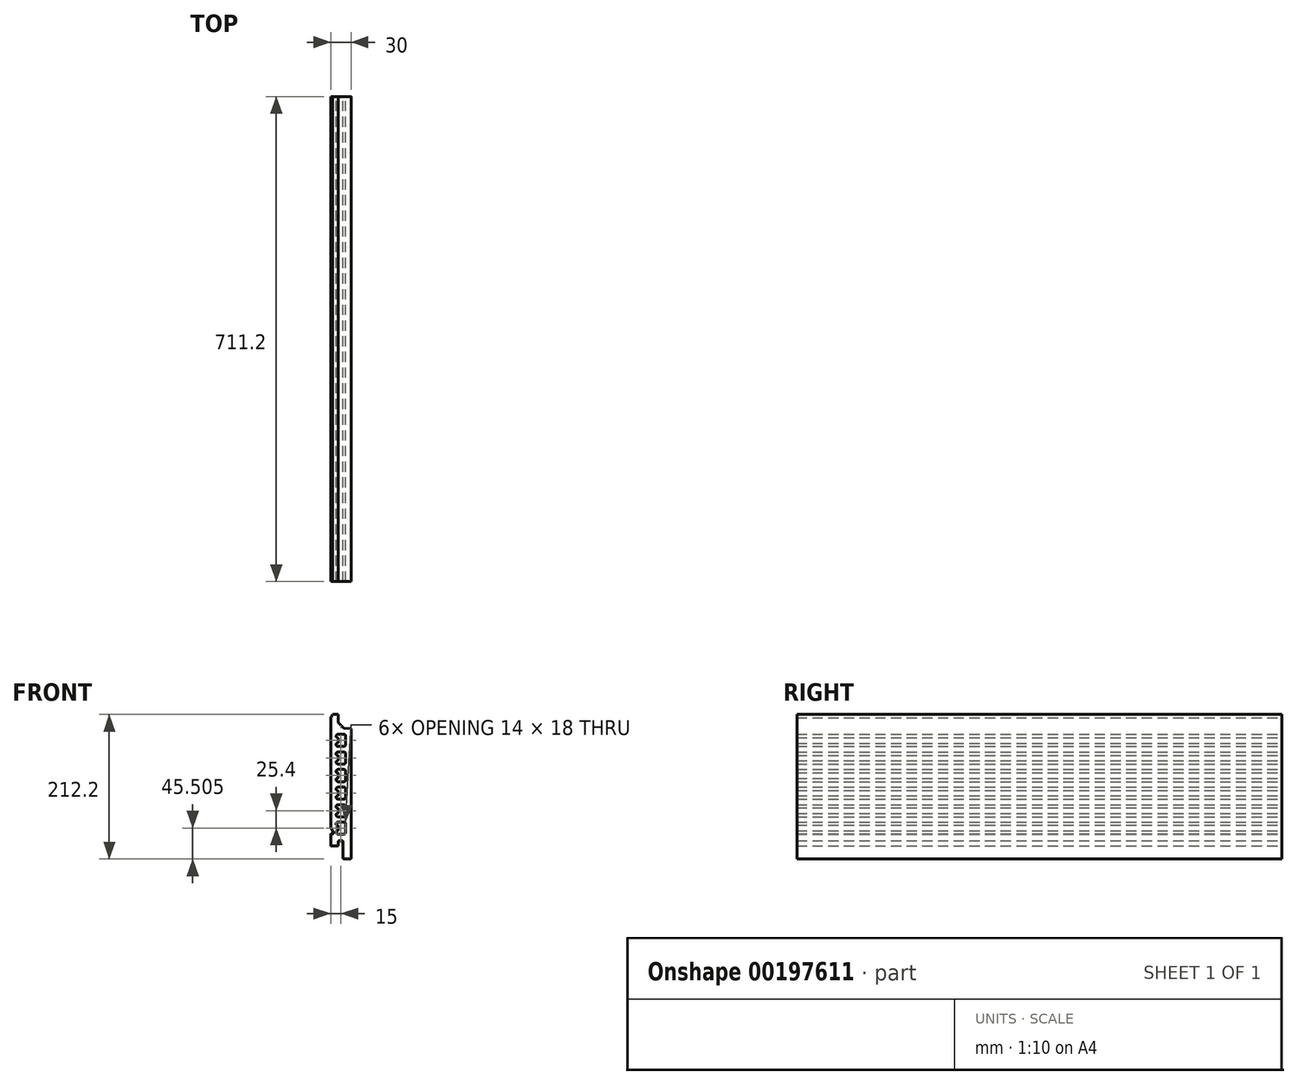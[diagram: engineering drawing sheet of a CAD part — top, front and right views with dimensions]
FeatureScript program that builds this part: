
annotation { "Feature Type Name" : "Feature", "Feature Type Description" : "" }
export const myFeature = defineFeature(function(context is Context, id is Id, definition is map)
    precondition{}
    {
        {
            var Q0;
            Q0=qCreatedBy(makeId("Front.planeOp"),FACE);
            var sketch = newSketch(context, id + "F0", { "sketchPlane" : qUnion([Q0])});
            skLineSegment(sketch, "E0", {"start": v(-14.86, -59.63) * mm, "end": v(-11.1, -67.7) * mm});
            skArc(sketch, "E1", {"start": v(-11.1, -67.7) * mm, "mid": v(-11.16, -68.66) * mm, "end": v(-12, -69.12) * mm});
            skLineSegment(sketch, "E2", {"start": v(-12, -69.12) * mm, "end": v(-14, -69.12) * mm});
            skArc(sketch, "E3", {"start": v(-14, -69.12) * mm, "mid": v(-14.7, -69.41) * mm, "end": v(-15, -70.12) * mm});
            skLineSegment(sketch, "E4", {"start": v(-15, -70.12) * mm, "end": v(-15, -85.6) * mm});
            skArc(sketch, "E5", {"start": v(-15, -85.6) * mm, "mid": v(-14.56, -86.66) * mm, "end": v(-13.5, -87.1) * mm});
            skLineSegment(sketch, "E6", {"start": v(-13.5, -87.1) * mm, "end": v(-5.5, -87.1) * mm});
            skArc(sketch, "E7", {"start": v(-5.5, -87.1) * mm, "mid": v(-4.44, -86.66) * mm, "end": v(-4, -85.6) * mm});
            skLineSegment(sketch, "E8", {"start": v(-4, -85.6) * mm, "end": v(-4, -80.6) * mm});
            skArc(sketch, "E9", {"start": v(-4, -80.6) * mm, "mid": v(-3.56, -79.54) * mm, "end": v(-2.5, -79.1) * mm});
            skLineSegment(sketch, "E10", {"start": v(-2.5, -79.1) * mm, "end": v(1.48, -79.1) * mm});
            skArc(sketch, "E11", {"start": v(1.48, -79.1) * mm, "mid": v(2.54, -79.54) * mm, "end": v(2.98, -80.6) * mm});
            skLineSegment(sketch, "E12", {"start": v(2.98, -80.6) * mm, "end": v(2.98, -104.6) * mm});
            skArc(sketch, "E13", {"start": v(2.98, -104.6) * mm, "mid": v(3.42, -105.66) * mm, "end": v(4.48, -106.1) * mm});
            skLineSegment(sketch, "E14", {"start": v(4.48, -106.1) * mm, "end": v(13.5, -106.1) * mm});
            skArc(sketch, "E15", {"start": v(13.5, -106.1) * mm, "mid": v(14.56, -105.66) * mm, "end": v(15, -104.6) * mm});
            skLineSegment(sketch, "E16", {"start": v(15, -104.6) * mm, "end": v(15, 83.78) * mm});
            skArc(sketch, "E17", {"start": v(15, 83.78) * mm, "mid": v(14.58, 84.81) * mm, "end": v(13.57, 85.27) * mm});
            skLineSegment(sketch, "E18", {"start": v(13.57, 85.27) * mm, "end": v(5.1, 85.66) * mm});
            skArc(sketch, "E19", {"start": v(5.1, 85.66) * mm, "mid": v(4.57, 85.79) * mm, "end": v(4.11, 86.1) * mm});
            skLineSegment(sketch, "E20", {"start": v(4.11, 86.1) * mm, "end": v(-3.56, 93.77) * mm});
            skArc(sketch, "E21", {"start": v(-3.56, 93.77) * mm, "mid": v(-3.89, 94.26) * mm, "end": v(-4, 94.83) * mm});
            skLineSegment(sketch, "E22", {"start": v(-4, 94.83) * mm, "end": v(-4, 106.1) * mm});
            skLineSegment(sketch, "E23", {"start": v(-4, 106.1) * mm, "end": v(-12.31, 106.1) * mm});
            skLineSegment(sketch, "E24", {"start": v(-12.31, 106.1) * mm, "end": v(-15, 101.2) * mm});
            skLineSegment(sketch, "E25", {"start": v(-15, 101.2) * mm, "end": v(-15, -59) * mm});
            skArc(sketch, "E26", {"start": v(-15, -59) * mm, "mid": v(-14.96, -59.32) * mm, "end": v(-14.86, -59.63) * mm});
            skArc(sketch, "E27", {"start": v(-14.86, -59.63) * mm, "mid": v(-14.96, -59.32) * mm, "end": v(-15, -59) * mm});
            skSolve(sketch);
        }
        {
            var Q0;
            Q0=makeQuery(id+"F0.imprint","IMPRINT",FACE,{"disambiguationData":[TD([[makeQuery(id+"F0.imprint","IMPRINT",EDGE,{"derivedFrom":sQuery(id+"F0.wireOp",EDGE,"E3")}),1.0]])]});
            extrude(context, id + "F1", {"entities" : qUnion([Q0]), "depth" : 711.2 * mm});
        }
        {
            var Q0;
            Q0=qCreatedBy(makeId("Front.planeOp"),FACE);
            var sketch = newSketch(context, id + "F2", { "sketchPlane" : qUnion([Q0])});
            skArc(sketch, "E28", {"start": v(-4, -32.7) * mm, "mid": v(-4.43, -31.63) * mm, "end": v(-5.5, -31.2) * mm});
            skLineSegment(sketch, "E29", {"start": v(-5.5, -31.2) * mm, "end": v(-5.5, -31.2) * mm});
            skArc(sketch, "E30", {"start": v(-5.5, -31.2) * mm, "mid": v(-6.56, -30.76) * mm, "end": v(-7, -29.7) * mm});
            skLineSegment(sketch, "E31", {"start": v(-7, -29.7) * mm, "end": v(-7, -29.2) * mm});
            skArc(sketch, "E32", {"start": v(-7, -29.2) * mm, "mid": v(-6.12, -27.07) * mm, "end": v(-4, -26.2) * mm});
            skLineSegment(sketch, "E33", {"start": v(-4, -26.2) * mm, "end": v(4, -26.2) * mm});
            skArc(sketch, "E34", {"start": v(4, -26.2) * mm, "mid": v(6.12, -27.07) * mm, "end": v(7, -29.2) * mm});
            skLineSegment(sketch, "E35", {"start": v(7, -29.2) * mm, "end": v(7, -41.2) * mm});
            skArc(sketch, "E36", {"start": v(7, -41.2) * mm, "mid": v(6.12, -43.32) * mm, "end": v(4, -44.2) * mm});
            skLineSegment(sketch, "E37", {"start": v(4, -44.2) * mm, "end": v(-4, -44.2) * mm});
            skArc(sketch, "E38", {"start": v(-4, -44.2) * mm, "mid": v(-6.12, -43.32) * mm, "end": v(-7, -41.2) * mm});
            skLineSegment(sketch, "E39", {"start": v(-7, -41.2) * mm, "end": v(-7, -40.7) * mm});
            skArc(sketch, "E40", {"start": v(-7, -40.7) * mm, "mid": v(-6.56, -39.63) * mm, "end": v(-5.5, -39.2) * mm});
            skLineSegment(sketch, "E41", {"start": v(-5.5, -39.2) * mm, "end": v(-5.5, -39.2) * mm});
            skArc(sketch, "E42", {"start": v(-5.5, -39.2) * mm, "mid": v(-4.43, -38.76) * mm, "end": v(-4, -37.7) * mm});
            skLineSegment(sketch, "E43", {"start": v(-4, -37.7) * mm, "end": v(-4, -32.7) * mm});
            skArc(sketch, "E44", {"start": v(-4, -58.1) * mm, "mid": v(-4.43, -57.03) * mm, "end": v(-5.5, -56.6) * mm});
            skLineSegment(sketch, "E45", {"start": v(-5.5, -56.6) * mm, "end": v(-5.5, -56.6) * mm});
            skArc(sketch, "E46", {"start": v(-5.5, -56.6) * mm, "mid": v(-6.56, -56.16) * mm, "end": v(-7, -55.1) * mm});
            skLineSegment(sketch, "E47", {"start": v(-7, -55.1) * mm, "end": v(-7, -54.6) * mm});
            skArc(sketch, "E48", {"start": v(-7, -54.6) * mm, "mid": v(-6.12, -52.47) * mm, "end": v(-4, -51.6) * mm});
            skLineSegment(sketch, "E49", {"start": v(-4, -51.6) * mm, "end": v(4, -51.6) * mm});
            skArc(sketch, "E50", {"start": v(4, -51.6) * mm, "mid": v(6.12, -52.47) * mm, "end": v(7, -54.6) * mm});
            skLineSegment(sketch, "E51", {"start": v(7, -54.6) * mm, "end": v(7, -66.6) * mm});
            skArc(sketch, "E52", {"start": v(7, -66.6) * mm, "mid": v(6.12, -68.72) * mm, "end": v(4, -69.6) * mm});
            skLineSegment(sketch, "E53", {"start": v(4, -69.6) * mm, "end": v(-4, -69.6) * mm});
            skArc(sketch, "E54", {"start": v(-4, -69.6) * mm, "mid": v(-6.12, -68.72) * mm, "end": v(-7, -66.6) * mm});
            skLineSegment(sketch, "E55", {"start": v(-7, -66.6) * mm, "end": v(-7, -66.1) * mm});
            skArc(sketch, "E56", {"start": v(-7, -66.1) * mm, "mid": v(-6.56, -65.03) * mm, "end": v(-5.5, -64.6) * mm});
            skLineSegment(sketch, "E57", {"start": v(-5.5, -64.6) * mm, "end": v(-5.5, -64.6) * mm});
            skArc(sketch, "E58", {"start": v(-5.5, -64.6) * mm, "mid": v(-4.43, -64.16) * mm, "end": v(-4, -63.1) * mm});
            skLineSegment(sketch, "E59", {"start": v(-4, -63.1) * mm, "end": v(-4, -58.1) * mm});
            skArc(sketch, "E60", {"start": v(-4, -6.9) * mm, "mid": v(-4.43, -5.83) * mm, "end": v(-5.5, -5.4) * mm});
            skLineSegment(sketch, "E61", {"start": v(-5.5, -5.4) * mm, "end": v(-5.5, -5.4) * mm});
            skArc(sketch, "E62", {"start": v(-5.5, -5.4) * mm, "mid": v(-6.56, -4.96) * mm, "end": v(-7, -3.9) * mm});
            skLineSegment(sketch, "E63", {"start": v(-7, -3.9) * mm, "end": v(-7, -3.4) * mm});
            skArc(sketch, "E64", {"start": v(-7, -3.4) * mm, "mid": v(-6.12, -1.27) * mm, "end": v(-4, -0.4) * mm});
            skLineSegment(sketch, "E65", {"start": v(-4, -0.4) * mm, "end": v(4, -0.4) * mm});
            skArc(sketch, "E66", {"start": v(4, -0.4) * mm, "mid": v(6.12, -1.27) * mm, "end": v(7, -3.4) * mm});
            skLineSegment(sketch, "E67", {"start": v(7, -3.4) * mm, "end": v(7, -15.4) * mm});
            skArc(sketch, "E68", {"start": v(7, -15.4) * mm, "mid": v(6.12, -17.52) * mm, "end": v(4, -18.4) * mm});
            skLineSegment(sketch, "E69", {"start": v(4, -18.4) * mm, "end": v(-4, -18.4) * mm});
            skArc(sketch, "E70", {"start": v(-4, -18.4) * mm, "mid": v(-6.12, -17.52) * mm, "end": v(-7, -15.4) * mm});
            skLineSegment(sketch, "E71", {"start": v(-7, -15.4) * mm, "end": v(-7, -14.9) * mm});
            skArc(sketch, "E72", {"start": v(-7, -14.9) * mm, "mid": v(-6.56, -13.83) * mm, "end": v(-5.5, -13.4) * mm});
            skLineSegment(sketch, "E73", {"start": v(-5.5, -13.4) * mm, "end": v(-5.5, -13.4) * mm});
            skArc(sketch, "E74", {"start": v(-5.5, -13.4) * mm, "mid": v(-4.43, -12.96) * mm, "end": v(-4, -11.9) * mm});
            skLineSegment(sketch, "E75", {"start": v(-4, -11.9) * mm, "end": v(-4, -6.9) * mm});
            skLineSegment(sketch, "E76", {"start": v(-5.5, 20.4) * mm, "end": v(-5.5, 20.4) * mm});
            skArc(sketch, "E77", {"start": v(-5.5, 20.4) * mm, "mid": v(-6.56, 20.84) * mm, "end": v(-7, 21.9) * mm});
            skLineSegment(sketch, "E78", {"start": v(-7, 21.9) * mm, "end": v(-7, 22.4) * mm});
            skArc(sketch, "E79", {"start": v(-7, 22.4) * mm, "mid": v(-6.12, 24.52) * mm, "end": v(-4, 25.4) * mm});
            skLineSegment(sketch, "E80", {"start": v(-4, 25.4) * mm, "end": v(4, 25.4) * mm});
            skArc(sketch, "E81", {"start": v(4, 25.4) * mm, "mid": v(6.12, 24.52) * mm, "end": v(7, 22.4) * mm});
            skLineSegment(sketch, "E82", {"start": v(7, 22.4) * mm, "end": v(7, 10.4) * mm});
            skArc(sketch, "E83", {"start": v(7, 10.4) * mm, "mid": v(6.12, 8.28) * mm, "end": v(4, 7.4) * mm});
            skLineSegment(sketch, "E84", {"start": v(4, 7.4) * mm, "end": v(-4, 7.4) * mm});
            skArc(sketch, "E85", {"start": v(-4, 7.4) * mm, "mid": v(-6.12, 8.28) * mm, "end": v(-7, 10.4) * mm});
            skLineSegment(sketch, "E86", {"start": v(-7, 10.4) * mm, "end": v(-7, 10.9) * mm});
            skArc(sketch, "E87", {"start": v(-7, 10.9) * mm, "mid": v(-6.56, 11.96) * mm, "end": v(-5.5, 12.4) * mm});
            skLineSegment(sketch, "E88", {"start": v(-5.5, 12.4) * mm, "end": v(-5.5, 12.4) * mm});
            skArc(sketch, "E89", {"start": v(-5.5, 12.4) * mm, "mid": v(-4.43, 12.84) * mm, "end": v(-4, 13.9) * mm});
            skLineSegment(sketch, "E90", {"start": v(-4, 13.9) * mm, "end": v(-4, 18.9) * mm});
            skArc(sketch, "E91", {"start": v(-4, 18.9) * mm, "mid": v(-4.43, 19.96) * mm, "end": v(-5.5, 20.4) * mm});
            skLineSegment(sketch, "E92", {"start": v(-5.5, 46.2) * mm, "end": v(-5.5, 46.2) * mm});
            skArc(sketch, "E93", {"start": v(-5.5, 46.2) * mm, "mid": v(-6.56, 46.64) * mm, "end": v(-7, 47.7) * mm});
            skLineSegment(sketch, "E94", {"start": v(-7, 47.7) * mm, "end": v(-7, 48.2) * mm});
            skArc(sketch, "E95", {"start": v(-7, 48.2) * mm, "mid": v(-6.12, 50.32) * mm, "end": v(-4, 51.2) * mm});
            skLineSegment(sketch, "E96", {"start": v(-4, 51.2) * mm, "end": v(4, 51.2) * mm});
            skArc(sketch, "E97", {"start": v(4, 51.2) * mm, "mid": v(6.12, 50.32) * mm, "end": v(7, 48.2) * mm});
            skLineSegment(sketch, "E98", {"start": v(7, 48.2) * mm, "end": v(7, 36.2) * mm});
            skArc(sketch, "E99", {"start": v(7, 36.2) * mm, "mid": v(6.12, 34.08) * mm, "end": v(4, 33.2) * mm});
            skLineSegment(sketch, "E100", {"start": v(4, 33.2) * mm, "end": v(-4, 33.2) * mm});
            skArc(sketch, "E101", {"start": v(-4, 33.2) * mm, "mid": v(-6.12, 34.08) * mm, "end": v(-7, 36.2) * mm});
            skLineSegment(sketch, "E102", {"start": v(-7, 36.2) * mm, "end": v(-7, 36.7) * mm});
            skArc(sketch, "E103", {"start": v(-7, 36.7) * mm, "mid": v(-6.56, 37.76) * mm, "end": v(-5.5, 38.2) * mm});
            skLineSegment(sketch, "E104", {"start": v(-5.5, 38.2) * mm, "end": v(-5.5, 38.2) * mm});
            skArc(sketch, "E105", {"start": v(-5.5, 38.2) * mm, "mid": v(-4.43, 38.64) * mm, "end": v(-4, 39.7) * mm});
            skLineSegment(sketch, "E106", {"start": v(-4, 39.7) * mm, "end": v(-4, 44.7) * mm});
            skArc(sketch, "E107", {"start": v(-4, 44.7) * mm, "mid": v(-4.43, 45.76) * mm, "end": v(-5.5, 46.2) * mm});
            skLineSegment(sketch, "E108", {"start": v(-5.5, 72) * mm, "end": v(-5.5, 72) * mm});
            skArc(sketch, "E109", {"start": v(-5.5, 72) * mm, "mid": v(-6.56, 72.43) * mm, "end": v(-7, 73.5) * mm});
            skLineSegment(sketch, "E110", {"start": v(-7, 73.5) * mm, "end": v(-7, 74) * mm});
            skArc(sketch, "E111", {"start": v(-7, 74) * mm, "mid": v(-6.12, 76.12) * mm, "end": v(-4, 77) * mm});
            skLineSegment(sketch, "E112", {"start": v(-4, 77) * mm, "end": v(4, 77) * mm});
            skArc(sketch, "E113", {"start": v(4, 77) * mm, "mid": v(6.12, 76.12) * mm, "end": v(7, 74) * mm});
            skLineSegment(sketch, "E114", {"start": v(7, 74) * mm, "end": v(7, 62) * mm});
            skArc(sketch, "E115", {"start": v(7, 62) * mm, "mid": v(6.12, 59.87) * mm, "end": v(4, 59) * mm});
            skLineSegment(sketch, "E116", {"start": v(4, 59) * mm, "end": v(-4, 59) * mm});
            skArc(sketch, "E117", {"start": v(-4, 59) * mm, "mid": v(-6.12, 59.87) * mm, "end": v(-7, 62) * mm});
            skLineSegment(sketch, "E118", {"start": v(-7, 62) * mm, "end": v(-7, 62.5) * mm});
            skArc(sketch, "E119", {"start": v(-7, 62.5) * mm, "mid": v(-6.56, 63.56) * mm, "end": v(-5.5, 64) * mm});
            skLineSegment(sketch, "E120", {"start": v(-5.5, 64) * mm, "end": v(-5.5, 64) * mm});
            skArc(sketch, "E121", {"start": v(-5.5, 64) * mm, "mid": v(-4.43, 64.43) * mm, "end": v(-4, 65.5) * mm});
            skLineSegment(sketch, "E122", {"start": v(-4, 65.5) * mm, "end": v(-4, 70.5) * mm});
            skArc(sketch, "E123", {"start": v(-4, 70.5) * mm, "mid": v(-4.43, 71.56) * mm, "end": v(-5.5, 72) * mm});
            skLineSegment(sketch, "E124", {"start": v(0, -69.6) * mm, "end": v(-0.5, -77) * mm});
            skSolve(sketch);
        }
        {
            var Q0;
            Q0 = qSketchRegion(id + "F2", true);
            extrude(context, id + "F3", {"entities" : qUnion([Q0]), "operationType" : NewBodyOperationType.REMOVE, "depth" : 711.2 * mm});
        }
    });
